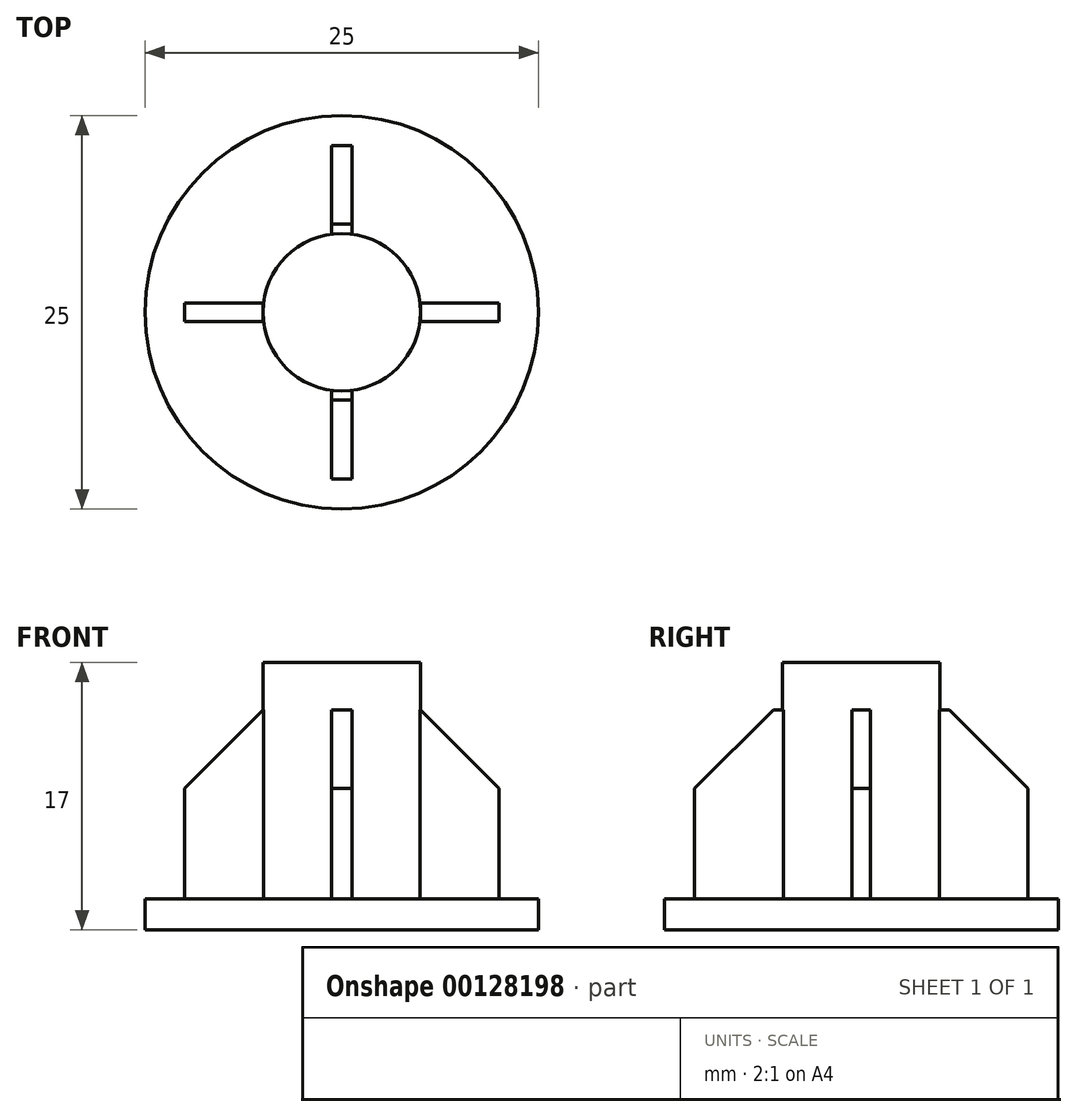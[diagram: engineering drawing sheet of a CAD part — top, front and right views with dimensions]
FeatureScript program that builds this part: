
annotation { "Feature Type Name" : "Feature", "Feature Type Description" : "" }
export const myFeature = defineFeature(function(context is Context, id is Id, definition is map)
    precondition{}
    {
        {
            var Q0;
            Q0=qCreatedBy(makeId("Top.planeOp"),FACE);
            var sketch = newSketch(context, id + "F0", { "sketchPlane" : qUnion([Q0])});
            skCircle(sketch, "E0", {"center": v(0, 0) * mm, "radius": 5 * mm});
            skSolve(sketch);
        }
        {
            var Q0;
            Q0=qCreatedBy(makeId("Top.planeOp"),FACE);
            var sketch = newSketch(context, id + "F1", { "sketchPlane" : qUnion([Q0])});
            skLineSegment(sketch, "E1.bottom", {"start": v(10, -0.59) * mm, "end": v(-10, -0.59) * mm});
            skLineSegment(sketch, "E1.top", {"start": v(10, 0.59) * mm, "end": v(-10, 0.59) * mm});
            skLineSegment(sketch, "E1.left", {"start": v(10, -0.59) * mm, "end": v(10, 0.59) * mm});
            skLineSegment(sketch, "E1.right", {"start": v(-10, -0.59) * mm, "end": v(-10, 0.59) * mm});
            skPoint(sketch, "E1.middle", {"position": v(0, 0) * mm});
            skLineSegment(sketch, "E2.bottom", {"start": v(0.66, 10.59) * mm, "end": v(-0.66, 10.59) * mm});
            skLineSegment(sketch, "E2.top", {"start": v(0.66, -10.59) * mm, "end": v(-0.66, -10.59) * mm});
            skLineSegment(sketch, "E2.left", {"start": v(0.66, 10.59) * mm, "end": v(0.66, -10.59) * mm});
            skLineSegment(sketch, "E2.right", {"start": v(-0.66, 10.59) * mm, "end": v(-0.66, -10.59) * mm});
            skSolve(sketch);
        }
        {
            var Q0;
            Q0=makeQuery(id+"F0.imprint","IMPRINT",FACE,{"disambiguationData":[TD([[makeQuery(id+"F0.imprint","IMPRINT",EDGE,{"derivedFrom":sQuery(id+"F0.wireOp",EDGE,"E0")}),1.0]])]});
            extrude(context, id + "F2", {"entities" : qUnion([Q0]), "depth" : 15 * mm});
        }
        {
            var Q0;
            {var subQ0=sQuery(id+"F1.wireOp",EDGE,"E1.left");Q0=makeQuery(id+"F1.imprint","IMPRINT",FACE,{"disambiguationData":[TD([[makeQuery(id+"F1.imprint","IMPRINT",EDGE,{"derivedFrom":subQ0}),1.0]])]});}
            var Q1;
            {var subQ0=sQuery(id+"F1.wireOp",EDGE,"E1.right");Q1=makeQuery(id+"F1.imprint","IMPRINT",FACE,{"disambiguationData":[TD([[makeQuery(id+"F1.imprint","IMPRINT",EDGE,{"derivedFrom":subQ0}),-1.0]])]});}
            var Q2;
            {var subQ5=sQuery(id+"F1.wireOp",EDGE,"E2.bottom");Q2=makeQuery(id+"F1.imprint","IMPRINT",FACE,{"disambiguationData":[TD([[makeQuery(id+"F1.imprint","IMPRINT",EDGE,{"derivedFrom":subQ5}),1.0]])]});}
            var Q3;
            {var subQ5=sQuery(id+"F1.wireOp",EDGE,"E2.top");Q3=makeQuery(id+"F1.imprint","IMPRINT",FACE,{"disambiguationData":[TD([[makeQuery(id+"F1.imprint","IMPRINT",EDGE,{"derivedFrom":subQ5}),-1.0]])]});}
            extrude(context, id + "F3", {"entities" : qUnion([Q0, Q1, Q2, Q3]), "operationType" : NewBodyOperationType.ADD, "depth" : 12 * mm});
        }
        {
            var Q0;
            Q0=makeQuery(id+"F3.opExtrude","CAP_EDGE",EDGE,{"disambiguationData":[OSD([sQuery(id+"F1.wireOp",EDGE,"E2.bottom")])],"isStart":false});
            var Q1;
            Q1=makeQuery(id+"F3.opExtrude","CAP_EDGE",EDGE,{"disambiguationData":[OSD([sQuery(id+"F1.wireOp",EDGE,"E1.left")])],"isStart":false});
            var Q2;
            Q2=makeQuery(id+"F3.opExtrude","CAP_EDGE",EDGE,{"disambiguationData":[OSD([sQuery(id+"F1.wireOp",EDGE,"E2.top")])],"isStart":false});
            var Q3;
            Q3=makeQuery(id+"F3.opExtrude","CAP_EDGE",EDGE,{"disambiguationData":[OSD([sQuery(id+"F1.wireOp",EDGE,"E1.right")])],"isStart":false});
            chamfer(context, id + "F4", {"entities" : qUnion([Q0, Q1, Q2, Q3]), "width" : 5 * mm, "tangentPropagation" : true});
        }
        {
            var Q0;
            Q0=qCreatedBy(makeId("Top.planeOp"),FACE);
            var sketch = newSketch(context, id + "F5", { "sketchPlane" : qUnion([Q0])});
            skCircle(sketch, "E3", {"center": v(0, 0) * mm, "radius": 12.5 * mm});
            skSolve(sketch);
        }
        {
            var Q0;
            Q0=makeQuery(id+"F5.imprint","IMPRINT",FACE,{"disambiguationData":[TD([[makeQuery(id+"F5.imprint","IMPRINT",EDGE,{"derivedFrom":sQuery(id+"F5.wireOp",EDGE,"E3")}),1.0]])]});
            extrude(context, id + "F6", {"entities" : qUnion([Q0]), "operationType" : NewBodyOperationType.ADD, "oppositeDirection" : true, "depth" : 2 * mm});
        }
    });
